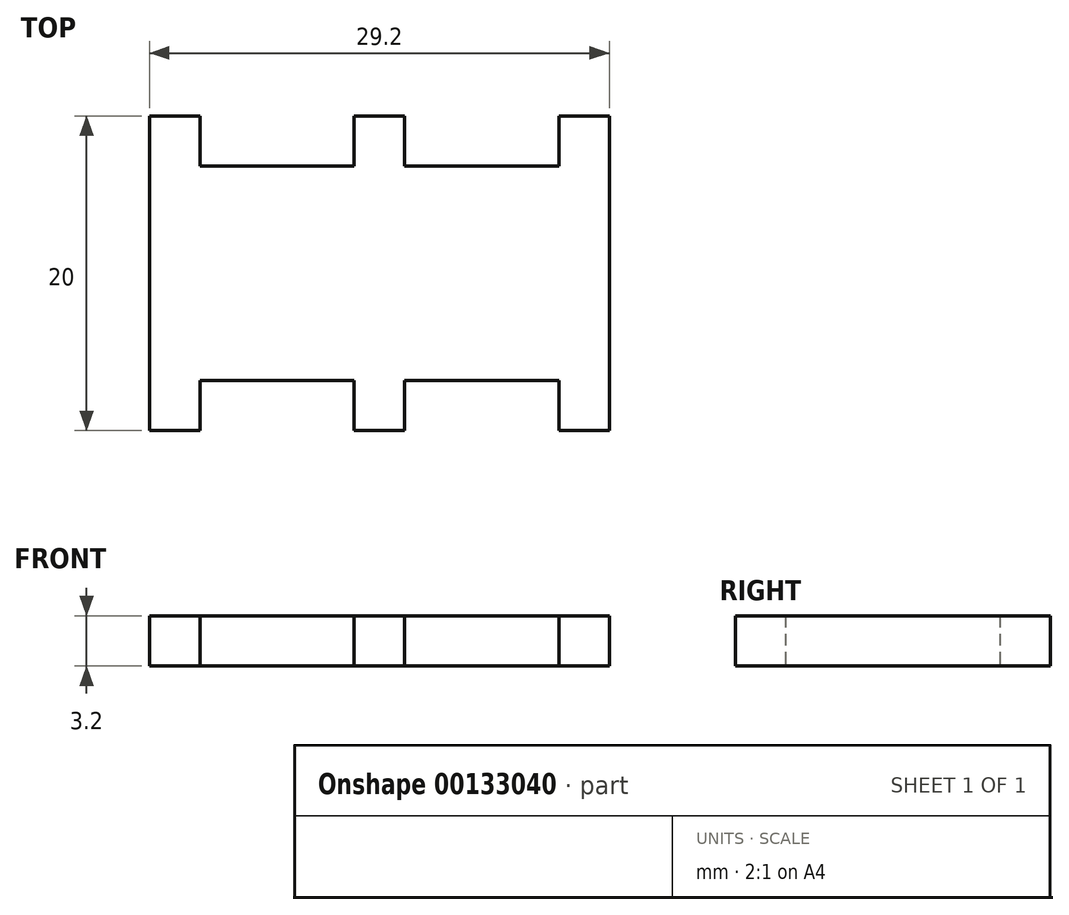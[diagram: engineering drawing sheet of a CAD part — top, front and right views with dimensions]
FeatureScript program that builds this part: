
annotation { "Feature Type Name" : "Feature", "Feature Type Description" : "" }
export const myFeature = defineFeature(function(context is Context, id is Id, definition is map)
    precondition{}
    {
        {
            var Q0;
            Q0=qCreatedBy(makeId("Top.planeOp"),FACE);
            var sketch = newSketch(context, id + "F0", { "sketchPlane" : qUnion([Q0])});
            skLineSegment(sketch, "E0.bottom", {"start": v(1.6, 10) * mm, "end": v(-1.6, 10) * mm});
            skLineSegment(sketch, "E0.top", {"start": v(1.6, -10) * mm, "end": v(-1.6, -10) * mm});
            skLineSegment(sketch, "E0.left", {"start": v(1.6, 10) * mm, "end": v(1.6, 6.8) * mm});
            skLineSegment(sketch, "E0.right", {"start": v(-1.6, 10) * mm, "end": v(-1.6, -10) * mm});
            skPoint(sketch, "E0.middle", {"position": v(0, 0) * mm});
            skLineSegment(sketch, "E1", {"start": v(1.6, -10) * mm, "end": v(1.6, -6.8) * mm, "construction": true});
            skLineSegment(sketch, "E2", {"start": v(1.6, -6.8) * mm, "end": v(11.4, -6.8) * mm});
            skLineSegment(sketch, "E3", {"start": v(24.4, -6.8) * mm, "end": v(24.4, -10) * mm});
            skLineSegment(sketch, "E4", {"start": v(24.4, -10) * mm, "end": v(27.6, -10) * mm});
            skLineSegment(sketch, "E5", {"start": v(27.6, -10) * mm, "end": v(27.6, 10) * mm});
            skLineSegment(sketch, "E6", {"start": v(27.6, 10) * mm, "end": v(24.4, 10) * mm});
            skLineSegment(sketch, "E7", {"start": v(24.4, 10) * mm, "end": v(24.4, 6.8) * mm});
            skLineSegment(sketch, "E8", {"start": v(24.4, 6.8) * mm, "end": v(14.6, 6.8) * mm});
            skLineSegment(sketch, "E9.trimOffspring", {"start": v(1.6, -6.8) * mm, "end": v(1.6, -10) * mm});
            skLineSegment(sketch, "E10", {"start": v(24.4, 6.8) * mm, "end": v(14.6, 6.8) * mm, "construction": true});
            skLineSegment(sketch, "E11", {"start": v(14.6, 6.8) * mm, "end": v(14.6, 10) * mm});
            skLineSegment(sketch, "E12", {"start": v(14.6, 10) * mm, "end": v(11.4, 10) * mm});
            skLineSegment(sketch, "E13", {"start": v(11.4, 10) * mm, "end": v(11.4, 6.8) * mm});
            skLineSegment(sketch, "E14.trimOffspring", {"start": v(11.4, 6.8) * mm, "end": v(1.6, 6.8) * mm});
            skLineSegment(sketch, "E15", {"start": v(24.4, -6.8) * mm, "end": v(14.6, -6.8) * mm, "construction": true});
            skLineSegment(sketch, "E16", {"start": v(14.6, -6.8) * mm, "end": v(14.6, -10) * mm});
            skLineSegment(sketch, "E17", {"start": v(14.6, -10) * mm, "end": v(11.4, -10) * mm});
            skLineSegment(sketch, "E18", {"start": v(11.4, -10) * mm, "end": v(11.4, -6.8) * mm});
            skLineSegment(sketch, "E19.trimOffspring", {"start": v(14.6, -6.8) * mm, "end": v(24.4, -6.8) * mm});
            skSolve(sketch);
        }
        {
            var Q0;
            Q0=makeQuery(id+"F0.imprint","IMPRINT",FACE,{"disambiguationData":[TD([[makeQuery(id+"F0.imprint","IMPRINT",EDGE,{"derivedFrom":sQuery(id+"F0.wireOp",EDGE,"E0.bottom")}),1.0]])]});
            extrude(context, id + "F1", {"entities" : qUnion([Q0]), "endBound" : BoundingType.SYMMETRIC, "depth" : 3.2 * mm});
        }
    });
